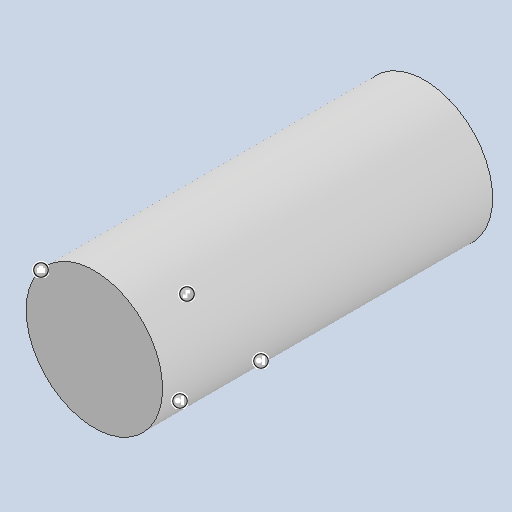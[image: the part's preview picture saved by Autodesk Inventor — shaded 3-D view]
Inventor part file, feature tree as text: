
AUTODESK INVENTOR PART (.ipt)
format: ipt  version: 2024 (Build 280153000, 153)  size: 205,824 bytes
history: native  units: mm
features: extrude x1
ambient origin geometry x8: Origin, YZ Plane, XZ Plane, XY Plane, X Axis, Y Axis, Z Axis, Center Point
bodies: Solid1 (feature_tree)
feature tree (1):
  extrude  "Extrusion1"  TaperAngle=0.0deg  [1 undecoded]
note: 1 required parameter value undecoded (feature->parameter linkage not recoverable at this tier; creation-order binding heuristic only, values carry confidence <= 0.55)
